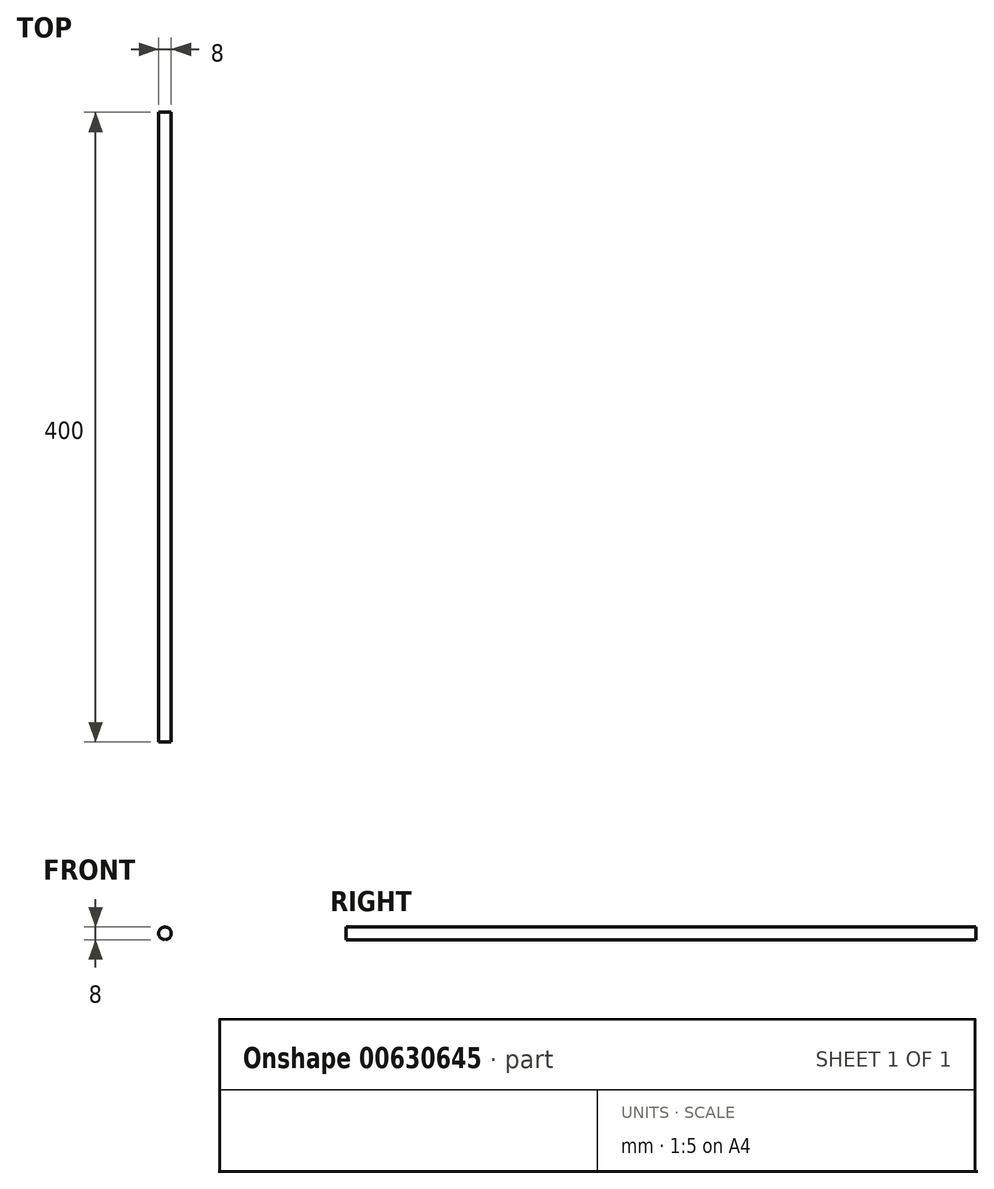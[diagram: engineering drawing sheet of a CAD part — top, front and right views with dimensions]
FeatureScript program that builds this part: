
annotation { "Feature Type Name" : "Feature", "Feature Type Description" : "" }
export const myFeature = defineFeature(function(context is Context, id is Id, definition is map)
    precondition{}
    {
        {
            var Q0;
            Q0=qCreatedBy(makeId("Front.planeOp"),FACE);
            var sketch = newSketch(context, id + "F0", { "sketchPlane" : qUnion([Q0])});
            skCircle(sketch, "E0", {"center": v(0, 0) * mm, "radius": 4 * mm});
            skSolve(sketch);
        }
        {
            var Q0;
            Q0=makeQuery(id+"F0.imprint","IMPRINT",FACE,{"disambiguationData":[TD([[makeQuery(id+"F0.imprint","IMPRINT",EDGE,{"derivedFrom":sQuery(id+"F0.wireOp",EDGE,"E0")}),1.0]])]});
            extrude(context, id + "F1", {"entities" : qUnion([Q0]), "depth" : 400 * mm, "offsetDistance" : 25 * mm});
        }
    });
